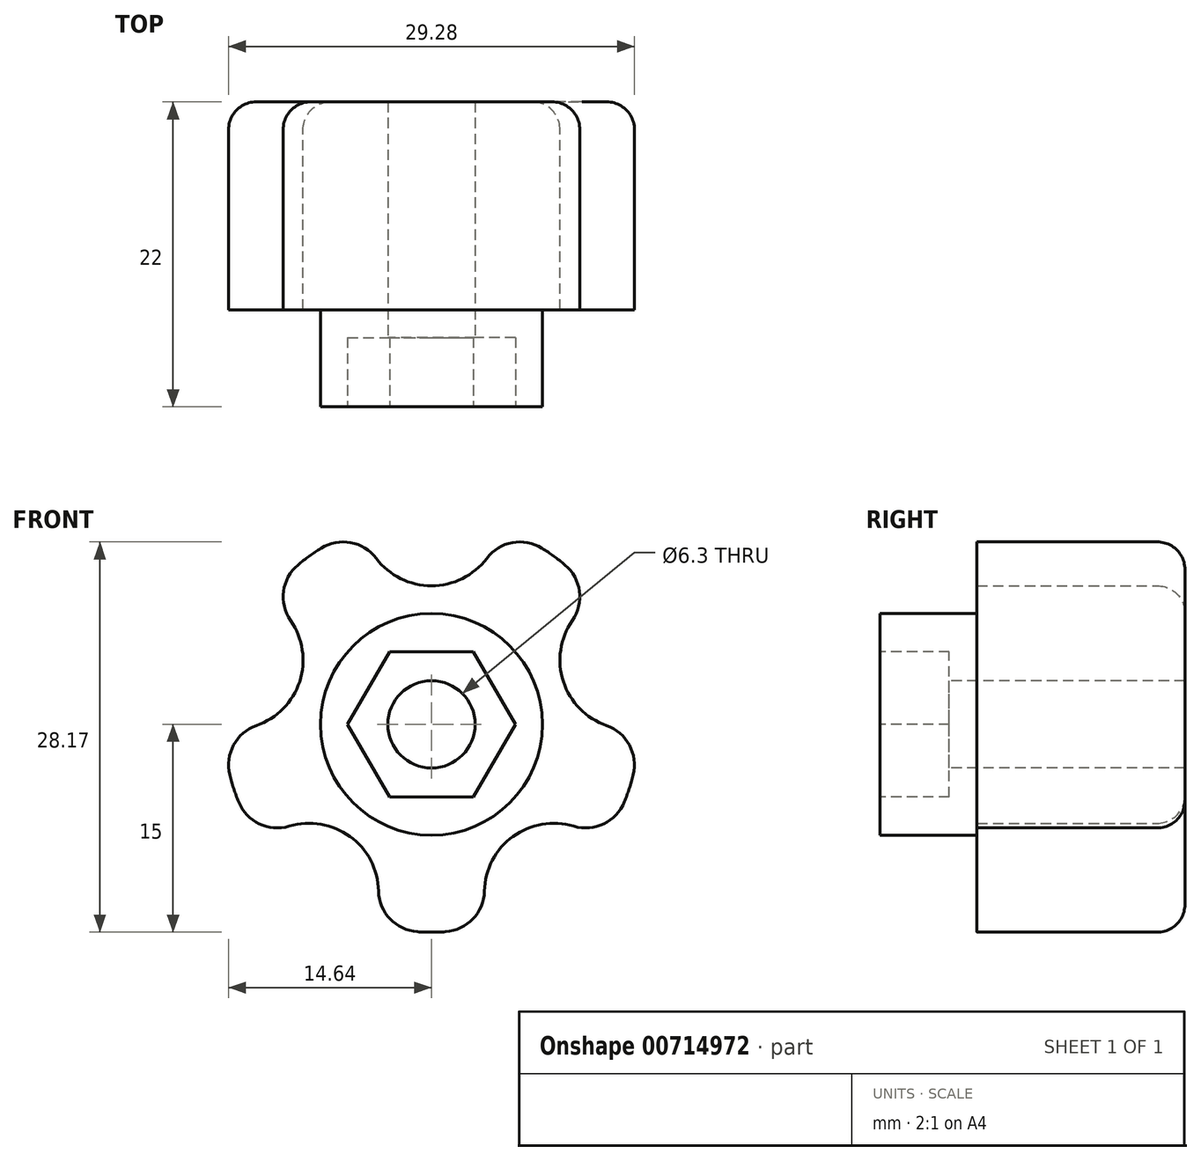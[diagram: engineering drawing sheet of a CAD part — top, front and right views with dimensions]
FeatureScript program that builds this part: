
annotation { "Feature Type Name" : "Feature", "Feature Type Description" : "" }
export const myFeature = defineFeature(function(context is Context, id is Id, definition is map)
    precondition{}
    {
        {
            var Q0;
            Q0=qCreatedBy(makeId("Right.planeOp"),FACE);
            var sketch = newSketch(context, id + "F0", { "sketchPlane" : qUnion([Q0])});
            skLineSegment(sketch, "E0", {"start": v(0, 0) * mm, "end": v(0, 15) * mm});
            skLineSegment(sketch, "E1", {"start": v(0, 15) * mm, "end": v(-15, 15) * mm});
            skLineSegment(sketch, "E2", {"start": v(-15, 15) * mm, "end": v(-15, 8) * mm});
            skLineSegment(sketch, "E3", {"start": v(-15, 8) * mm, "end": v(-22, 8) * mm});
            skLineSegment(sketch, "E4", {"start": v(0, 0) * mm, "end": v(-22, 0) * mm});
            skLineSegment(sketch, "E5", {"start": v(-22, 8) * mm, "end": v(-22, 0) * mm});
            skSolve(sketch);
        }
        {
            var Q0;
            Q0 = qSketchRegion(id + "F0", true);
            var Q1;
            Q1=sQuery(id+"F0.wireOp",EDGE,"E4");
            revolve(context, id + "F1", {"surfaceOperationType" : NewSurfaceOperationType.NEW, "entities" : qUnion([Q0]), "axis" : qUnion([Q1]), "revolveType" : RevolveType.FULL});
        }
        {
            var Q0;
            Q0=makeQuery(id+"F1.opRevolve","SWEPT_FACE",FACE,{"disambiguationData":[OSD([sQuery(id+"F0.wireOp",EDGE,"E0")])]});
            var sketch = newSketch(context, id + "F2", { "sketchPlane" : qUnion([Q0])});
            skCircle(sketch, "E6", {"center": v(0, 15) * mm, "radius": 5 * mm});
            skCircle(sketch, "E7.1.0", {"center": v(-14.27, 4.64) * mm, "radius": 5 * mm});
            skCircle(sketch, "E7.2.0", {"center": v(-8.82, -12.14) * mm, "radius": 5 * mm});
            skCircle(sketch, "E7.3.0", {"center": v(8.82, -12.14) * mm, "radius": 5 * mm});
            skCircle(sketch, "E7.4.0", {"center": v(14.27, 4.64) * mm, "radius": 5 * mm});
            skPoint(sketch, "E7.center", {"position": v(0, 0) * mm});
            skSolve(sketch);
        }
        {
            var Q0;
            Q0 = qSketchRegion(id + "F2", true);
            extrude(context, id + "F3", {"entities" : qUnion([Q0]), "operationType" : NewBodyOperationType.REMOVE, "oppositeDirection" : true, "depth" : 15 * mm, "offsetDistance" : 25 * mm});
        }
        {
            var Q0;
            Q0=makeQuery(id+"F3.boolean.opBoolean","INTERSECT",EDGE,{"disambiguationData":[OD(0.0)],"derivedFrom":[makeQuery(id+"F1.opRevolve","SWEPT_FACE",FACE,{"disambiguationData":[OSD([sQuery(id+"F0.wireOp",EDGE,"E1")])]}),makeQuery(id+"F3.opExtrude","SWEPT_FACE",FACE,{"disambiguationData":[OSD([sQuery(id+"F2.wireOp",EDGE,"E7.1.0")])]})]});
            var Q1;
            Q1=makeQuery(id+"F3.boolean.opBoolean","INTERSECT",EDGE,{"disambiguationData":[OD(1.0)],"derivedFrom":[makeQuery(id+"F1.opRevolve","SWEPT_FACE",FACE,{"disambiguationData":[OSD([sQuery(id+"F0.wireOp",EDGE,"E1")])]}),makeQuery(id+"F3.opExtrude","SWEPT_FACE",FACE,{"disambiguationData":[OSD([sQuery(id+"F2.wireOp",EDGE,"E7.1.0")])]})]});
            var Q2;
            Q2=makeQuery(id+"F3.boolean.opBoolean","INTERSECT",EDGE,{"disambiguationData":[OD(0.0)],"derivedFrom":[makeQuery(id+"F1.opRevolve","SWEPT_FACE",FACE,{"disambiguationData":[OSD([sQuery(id+"F0.wireOp",EDGE,"E1")])]}),makeQuery(id+"F3.opExtrude","SWEPT_FACE",FACE,{"disambiguationData":[OSD([sQuery(id+"F2.wireOp",EDGE,"E7.2.0")])]})]});
            var Q3;
            Q3=makeQuery(id+"F3.boolean.opBoolean","INTERSECT",EDGE,{"disambiguationData":[OD(1.0)],"derivedFrom":[makeQuery(id+"F1.opRevolve","SWEPT_FACE",FACE,{"disambiguationData":[OSD([sQuery(id+"F0.wireOp",EDGE,"E1")])]}),makeQuery(id+"F3.opExtrude","SWEPT_FACE",FACE,{"disambiguationData":[OSD([sQuery(id+"F2.wireOp",EDGE,"E7.2.0")])]})]});
            var Q4;
            Q4=makeQuery(id+"F3.boolean.opBoolean","INTERSECT",EDGE,{"disambiguationData":[OD(0.0)],"derivedFrom":[makeQuery(id+"F1.opRevolve","SWEPT_FACE",FACE,{"disambiguationData":[OSD([sQuery(id+"F0.wireOp",EDGE,"E1")])]}),makeQuery(id+"F3.opExtrude","SWEPT_FACE",FACE,{"disambiguationData":[OSD([sQuery(id+"F2.wireOp",EDGE,"E7.3.0")])]})]});
            var Q5;
            Q5=makeQuery(id+"F3.boolean.opBoolean","INTERSECT",EDGE,{"disambiguationData":[OD(1.0)],"derivedFrom":[makeQuery(id+"F1.opRevolve","SWEPT_FACE",FACE,{"disambiguationData":[OSD([sQuery(id+"F0.wireOp",EDGE,"E1")])]}),makeQuery(id+"F3.opExtrude","SWEPT_FACE",FACE,{"disambiguationData":[OSD([sQuery(id+"F2.wireOp",EDGE,"E7.3.0")])]})]});
            var Q6;
            Q6=makeQuery(id+"F3.boolean.opBoolean","INTERSECT",EDGE,{"disambiguationData":[OD(1.0)],"derivedFrom":[makeQuery(id+"F1.opRevolve","SWEPT_FACE",FACE,{"disambiguationData":[OSD([sQuery(id+"F0.wireOp",EDGE,"E1")])]}),makeQuery(id+"F3.opExtrude","SWEPT_FACE",FACE,{"disambiguationData":[OSD([sQuery(id+"F2.wireOp",EDGE,"E7.4.0")])]})]});
            var Q7;
            Q7=makeQuery(id+"F3.boolean.opBoolean","INTERSECT",EDGE,{"disambiguationData":[OD(0.0)],"derivedFrom":[makeQuery(id+"F1.opRevolve","SWEPT_FACE",FACE,{"disambiguationData":[OSD([sQuery(id+"F0.wireOp",EDGE,"E1")])]}),makeQuery(id+"F3.opExtrude","SWEPT_FACE",FACE,{"disambiguationData":[OSD([sQuery(id+"F2.wireOp",EDGE,"E7.4.0")])]})]});
            var Q8;
            Q8=makeQuery(id+"F3.boolean.opBoolean","INTERSECT",EDGE,{"disambiguationData":[OD(1.0)],"derivedFrom":[makeQuery(id+"F1.opRevolve","SWEPT_FACE",FACE,{"disambiguationData":[OSD([sQuery(id+"F0.wireOp",EDGE,"E1")])]}),makeQuery(id+"F3.opExtrude","SWEPT_FACE",FACE,{"disambiguationData":[OSD([sQuery(id+"F2.wireOp",EDGE,"E6")])]})]});
            var Q9;
            Q9=makeQuery(id+"F3.boolean.opBoolean","INTERSECT",EDGE,{"disambiguationData":[OD(0.0)],"derivedFrom":[makeQuery(id+"F1.opRevolve","SWEPT_FACE",FACE,{"disambiguationData":[OSD([sQuery(id+"F0.wireOp",EDGE,"E1")])]}),makeQuery(id+"F3.opExtrude","SWEPT_FACE",FACE,{"disambiguationData":[OSD([sQuery(id+"F2.wireOp",EDGE,"E6")])]})]});
            fillet(context, id + "F4", {"entities" : qUnion([Q0, Q1, Q2, Q3, Q4, Q5, Q6, Q7, Q8, Q9]), "radius" : 3 * mm, "tangentPropagation" : true, "allowEdgeOverflow" : false});
        }
        {
            var Q0;
            Q0=makeQuery(id+"F1.opRevolve","SWEPT_FACE",FACE,{"disambiguationData":[OSD([sQuery(id+"F0.wireOp",EDGE,"E5")])]});
            var sketch = newSketch(context, id + "F5", { "sketchPlane" : qUnion([Q0])});
            skPoint(sketch, "E8", {"position": v(0, 0) * mm});
            skCircle(sketch, "E9.cCircle", {"center": v(0, 0) * mm, "radius": 5.25 * mm, "construction": true});
            skLineSegment(sketch, "E9.0", {"start": v(-3.03, 5.25) * mm, "end": v(3.03, 5.25) * mm});
            skLineSegment(sketch, "E9.1", {"start": v(3.03, 5.25) * mm, "end": v(6.06, 0) * mm});
            skLineSegment(sketch, "E9.2", {"start": v(6.06, 0) * mm, "end": v(3.03, -5.25) * mm});
            skLineSegment(sketch, "E9.3", {"start": v(3.03, -5.25) * mm, "end": v(-3.03, -5.25) * mm});
            skLineSegment(sketch, "E9.4", {"start": v(-3.03, -5.25) * mm, "end": v(-6.06, 0) * mm});
            skLineSegment(sketch, "E9.5", {"start": v(-6.06, 0) * mm, "end": v(-3.03, 5.25) * mm});
            skPoint(sketch, "E9.0.midPoint", {"position": v(0, 5.25) * mm});
            skSolve(sketch);
        }
        {
            var Q0;
            Q0 = qSketchRegion(id + "F5", true);
            extrude(context, id + "F6", {"entities" : qUnion([Q0]), "operationType" : NewBodyOperationType.REMOVE, "oppositeDirection" : true, "depth" : 5 * mm, "offsetDistance" : 25 * mm});
        }
        {
            var Q0;
            Q0=sQuery(id+"F5.wireOp",VERTEX,"E8");
            var Q1;
            Q1=makeQuery(id+"F1.opRevolve","SWEPT_BODY",BODY,{"disambiguationData":[OSD([sQuery(id+"F0.wireOp",EDGE,"E0"),sQuery(id+"F0.wireOp",EDGE,"E1"),sQuery(id+"F0.wireOp",EDGE,"E2"),sQuery(id+"F0.wireOp",EDGE,"E3"),sQuery(id+"F0.wireOp",EDGE,"E4"),sQuery(id+"F0.wireOp",EDGE,"E5")])]});
            hole(context, id + "F7", {"style" : HoleStyle.SIMPLE, "endStyle" : HoleEndStyle.THROUGH, "standardTappedOrClearance" : lookupTablePath({ "standard" : "ISO", "fit" : "Close", "size" : "M6", "type" : "Clearance" }), "standardBlindInLast" : lookupTablePath({ "fit" : "Close", "standard" : "ISO", "size" : "M6", "type" : "Clearance" }), "holeDiameter" : 6.3 * mm, "majorDiameter" : 5 * mm, "isTappedThrough" : true, "tappedDepth" : 12 * mm, "tapClearance" : 3, "locations" : qUnion([Q0]), "scope" : qUnion([Q1])});
        }
        {
            var Q0;
            Q0=makeQuery(id+"F4.opFillet","BLEND_EDGE",EDGE,{"blendedFrom":[makeQuery(id+"F3.boolean.opBoolean","INTERSECT",EDGE,{"disambiguationData":[OD(0.0)],"derivedFrom":[makeQuery(id+"F1.opRevolve","SWEPT_FACE",FACE,{"disambiguationData":[OSD([sQuery(id+"F0.wireOp",EDGE,"E1")])]}),makeQuery(id+"F3.opExtrude","SWEPT_FACE",FACE,{"disambiguationData":[OSD([sQuery(id+"F2.wireOp",EDGE,"E7.3.0")])]})]}),makeQuery(id+"F1.opRevolve","SWEPT_FACE",FACE,{"disambiguationData":[OSD([sQuery(id+"F0.wireOp",EDGE,"E0")])]})],"blendedInto":[makeQuery(id+"F1.opRevolve","SWEPT_FACE",FACE,{"disambiguationData":[OSD([sQuery(id+"F0.wireOp",EDGE,"E0")])]})]});
            fillet(context, id + "F8", {"entities" : qUnion([Q0]), "radius" : 2 * mm, "tangentPropagation" : true, "allowEdgeOverflow" : false});
        }
    });
